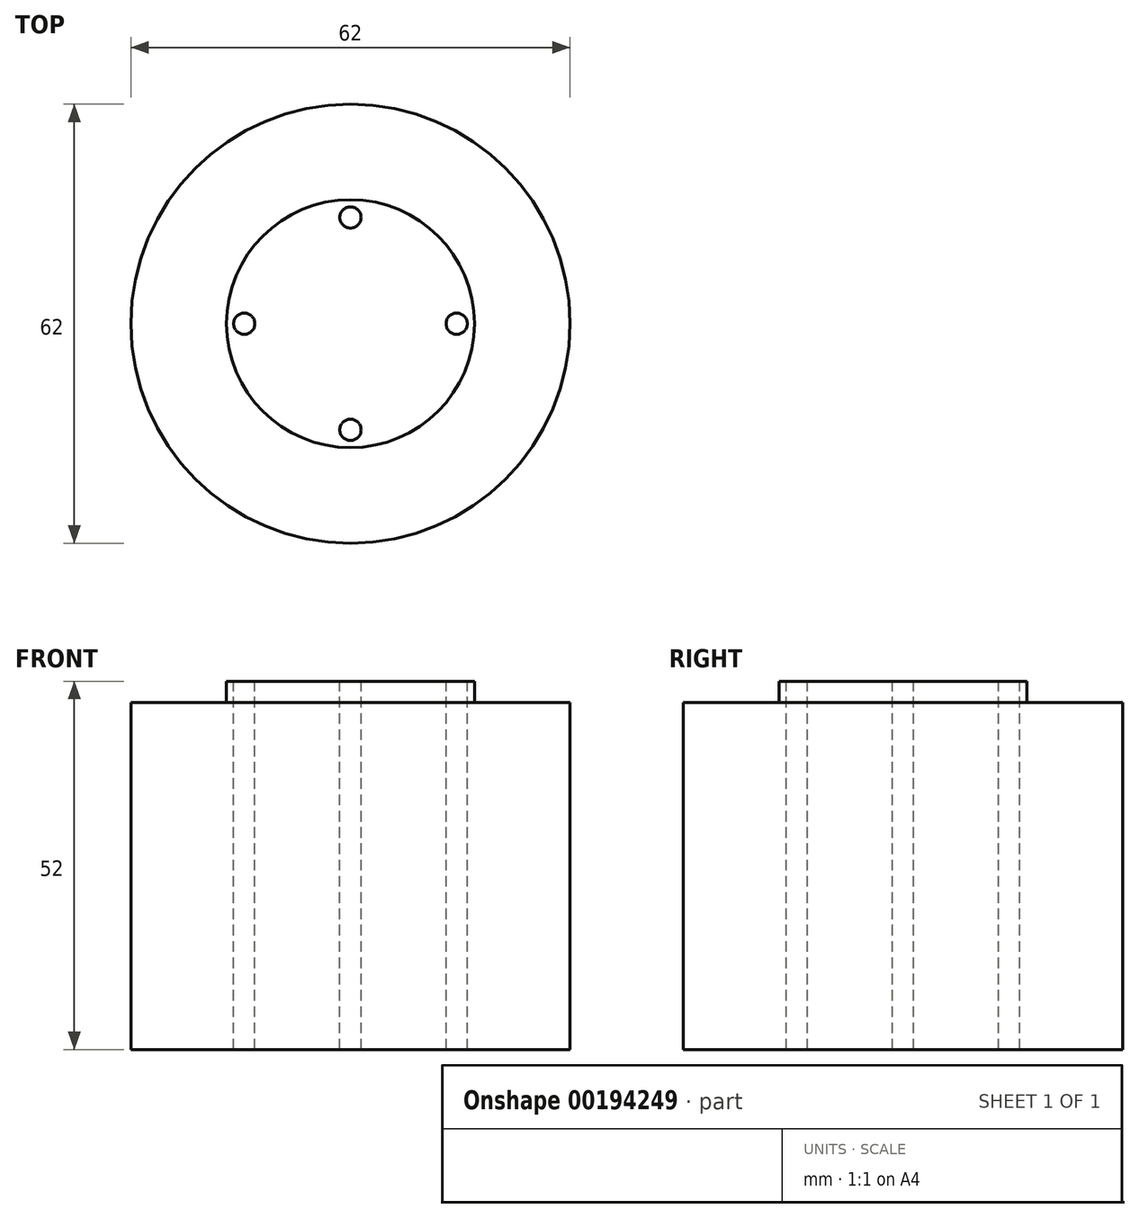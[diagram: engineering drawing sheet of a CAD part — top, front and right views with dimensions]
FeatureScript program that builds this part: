
annotation { "Feature Type Name" : "Feature", "Feature Type Description" : "" }
export const myFeature = defineFeature(function(context is Context, id is Id, definition is map)
    precondition{}
    {
        {
            var Q0;
            Q0=qCreatedBy(makeId("Top.planeOp"),FACE);
            var sketch = newSketch(context, id + "F0", { "sketchPlane" : qUnion([Q0])});
            skCircle(sketch, "E0", {"center": v(0, 0) * mm, "radius": 31 * mm});
            skSolve(sketch);
        }
        {
            var Q0;
            Q0=qSketchRegion(id+"F0",true);
            extrude(context, id + "F1", {"entities" : qUnion([Q0]), "depth" : 49 * mm});
        }
        {
            var Q0;
            Q0=qCreatedBy(makeId("Top.planeOp"),FACE);
            var sketch = newSketch(context, id + "F2", { "sketchPlane" : qUnion([Q0])});
            skCircle(sketch, "E1", {"center": v(0, 0) * mm, "radius": 17.5 * mm});
            skLineSegment(sketch, "E2", {"start": v(-15, 0) * mm, "end": v(0, 0) * mm});
            skLineSegment(sketch, "E3", {"start": v(0, 0) * mm, "end": v(15, 0) * mm});
            skLineSegment(sketch, "E4", {"start": v(0, 15) * mm, "end": v(0, 0) * mm});
            skLineSegment(sketch, "E5", {"start": v(0, 0) * mm, "end": v(0, -15) * mm});
            skSolve(sketch);
        }
        {
            var Q0;
            Q0=sQuery(id+"F2.wireOp",EDGE,"E1");
            extrude(context, id + "F3", {"bodyType" : ToolBodyType.SURFACE, "surfaceEntities" : qUnion([Q0]), "depth" : 4 * mm});
        }
        {
            var Q0;
            Q0=makeQuery(id+"F2.imprint","IMPRINT",FACE,{"disambiguationData":[TD([[makeQuery(id+"F2.imprint","IMPRINT",EDGE,{"derivedFrom":sQuery(id+"F2.wireOp",EDGE,"E1")}),1.0]])]});
            extrude(context, id + "F4", {"entities" : qUnion([Q0]), "operationType" : NewBodyOperationType.ADD, "depth" : 52 * mm});
        }
        {
            var Q0;
            Q0=makeQuery(id+"F4.opExtrude","CAP_FACE",FACE,{"disambiguationData":[OSD([sQuery(id+"F2.wireOp",EDGE,"E1")])],"isStart":false});
            var sketch = newSketch(context, id + "F5", { "sketchPlane" : qUnion([Q0])});
            skCircle(sketch, "E6", {"center": v(0, 15) * mm, "radius": 1.5 * mm});
            skCircle(sketch, "E7", {"center": v(-15, 0) * mm, "radius": 1.5 * mm});
            skCircle(sketch, "E8", {"center": v(15, 0) * mm, "radius": 1.5 * mm});
            skCircle(sketch, "E9", {"center": v(0, -15) * mm, "radius": 1.5 * mm});
            skCircle(sketch, "E10", {"center": v(0, 0) * mm, "radius": 7.5 * mm});
            skSolve(sketch);
        }
        {
            var Q0;
            Q0=sQuery(id+"F5.wireOp",VERTEX,"E6.center");
            var Q1;
            Q1=sQuery(id+"F5.wireOp",VERTEX,"E7.center");
            var Q2;
            Q2=sQuery(id+"F5.wireOp",VERTEX,"E9.center");
            var Q3;
            Q3=sQuery(id+"F5.wireOp",VERTEX,"E8.center");
            var Q4;
            Q4=makeQuery(id+"F1.opExtrude","SWEPT_BODY",BODY,{"disambiguationData":[OSD([sQuery(id+"F0.wireOp",EDGE,"E0")])]});
            hole(context, id + "F6", {"style" : HoleStyle.SIMPLE, "endStyle" : HoleEndStyle.THROUGH, "holeDiameter" : 3 * mm, "startFromSketch" : true, "locations" : qUnion([Q0, Q1, Q2, Q3]), "scope" : qUnion([Q4]), "isTappedThrough" : true});
        }
    });
